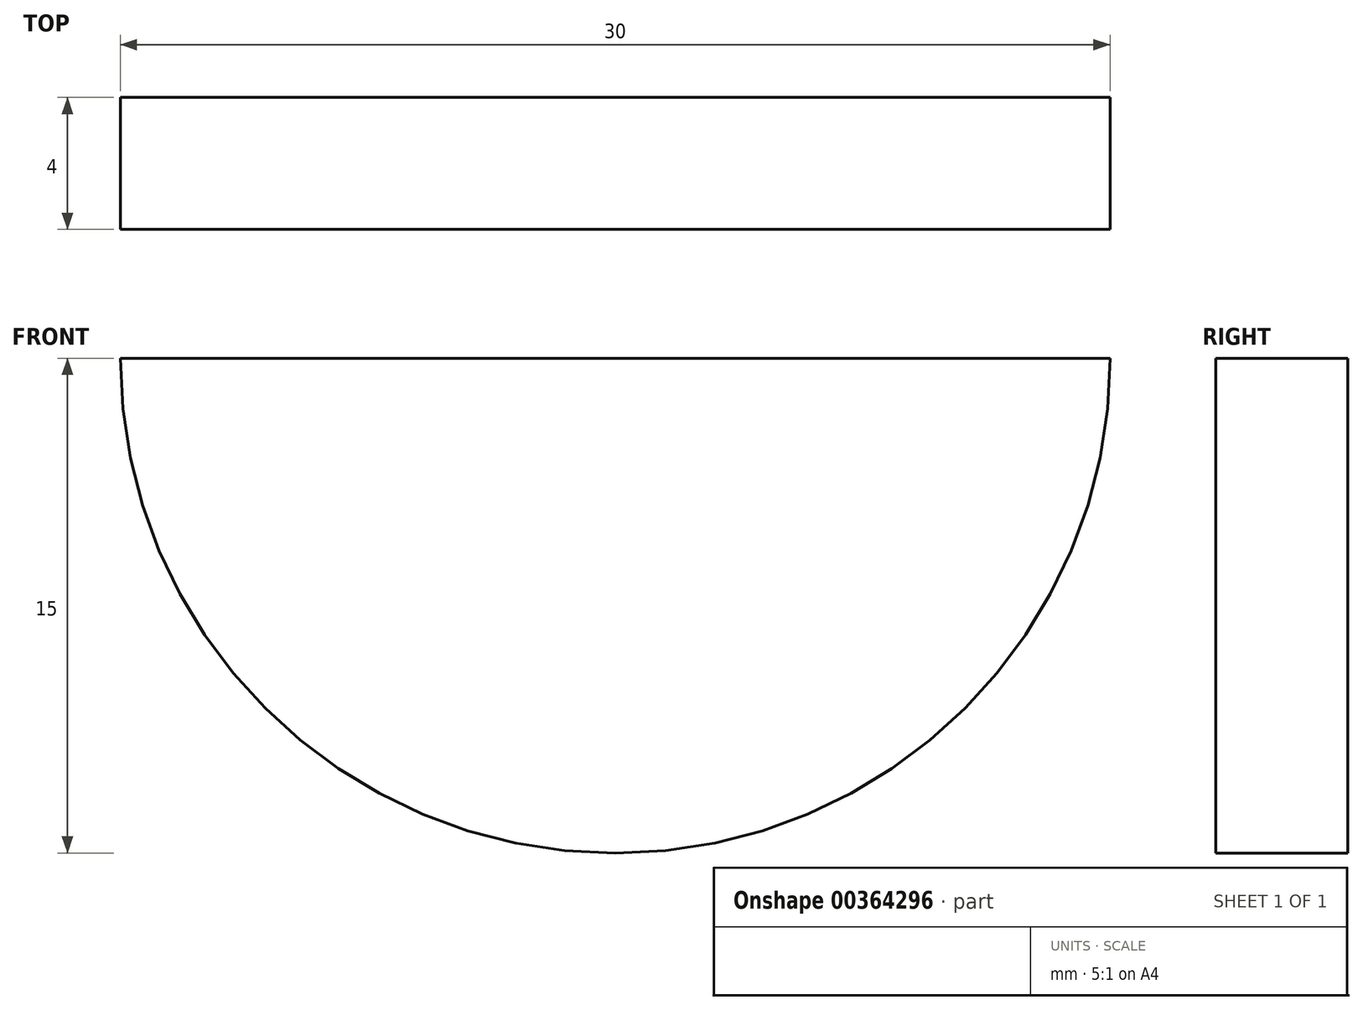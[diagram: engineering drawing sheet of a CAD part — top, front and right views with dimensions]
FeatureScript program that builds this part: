
annotation { "Feature Type Name" : "Feature", "Feature Type Description" : "" }
export const myFeature = defineFeature(function(context is Context, id is Id, definition is map)
    precondition{}
    {
        {
            var Q0;
            Q0=qCreatedBy(makeId("Front.planeOp"),FACE);
            var sketch = newSketch(context, id + "F0", { "sketchPlane" : qUnion([Q0])});
            skArc(sketch, "E0", {"start": v(-15, 0) * mm, "mid": v(0, -15) * mm, "end": v(15, 0) * mm});
            skLineSegment(sketch, "E1", {"start": v(-15, 0) * mm, "end": v(15, 0) * mm});
            skSolve(sketch);
        }
        {
            var Q0;
            Q0 = qSketchRegion(id + "F0", true);
            extrude(context, id + "F1", {"entities" : qUnion([Q0]), "oppositeDirection" : true, "depth" : 3 * mm, "offsetDistance" : 25 * mm});
        }
        {
            var Q0;
            Q0=makeQuery(id+"F1.opExtrude","CAP_FACE",FACE,{"disambiguationData":[OSD([sQuery(id+"F0.wireOp",EDGE,"E0"),sQuery(id+"F0.wireOp",EDGE,"E1")])],"isStart":true});
            var sketch = newSketch(context, id + "F2", { "sketchPlane" : qUnion([Q0])});
            skArc(sketch, "E2", {"start": v(18, 0) * mm, "mid": v(0, -18) * mm, "end": v(-18, 0) * mm});
            skLineSegment(sketch, "E3", {"start": v(-18, 0) * mm, "end": v(18, 0) * mm});
            skSolve(sketch);
        }
        {
            var Q0;
            {var subQ0=sQuery(id+"F2.wireOp",EDGE,"E2");Q0=makeQuery(id+"F2.imprint","IMPRINT",FACE,{"disambiguationData":[TD([[makeQuery(id+"F2.imprint","IMPRINT",EDGE,{"derivedFrom":subQ0}),-1.0]])]});}
            var Q1;
            {var subQ1=makeQuery(id+"F1.opExtrude","CAP_EDGE",EDGE,{"disambiguationData":[OSD([sQuery(id+"F0.wireOp",EDGE,"E0")])],"isStart":true});Q1=makeQuery(id+"F2.imprint","IMPRINT",FACE,{"disambiguationData":[TD([[makeQuery(id+"F2.imprint","IMPRINT",EDGE,{"derivedFrom":subQ1}),1.0]])]});}
            extrude(context, id + "F3", {"entities" : qUnion([Q0, Q1]), "operationType" : NewBodyOperationType.ADD, "depth" : 1 * mm, "offsetDistance" : 25 * mm});
        }
        {
            var Q0;
            Q0=makeQuery(id+"F3.opExtrude","CAP_FACE",FACE,{"disambiguationData":[OSD([sQuery(id+"F2.wireOp",EDGE,"E2"),sQuery(id+"F2.wireOp",EDGE,"E3")])],"isStart":false});
            cPlane(context, id + "F4", {"entities" : qUnion([Q0]), "cplaneType" : CPlaneType.OFFSET, "offset" : 12 * mm, "width" : 150 * mm, "height" : 150 * mm});
        }
    });
